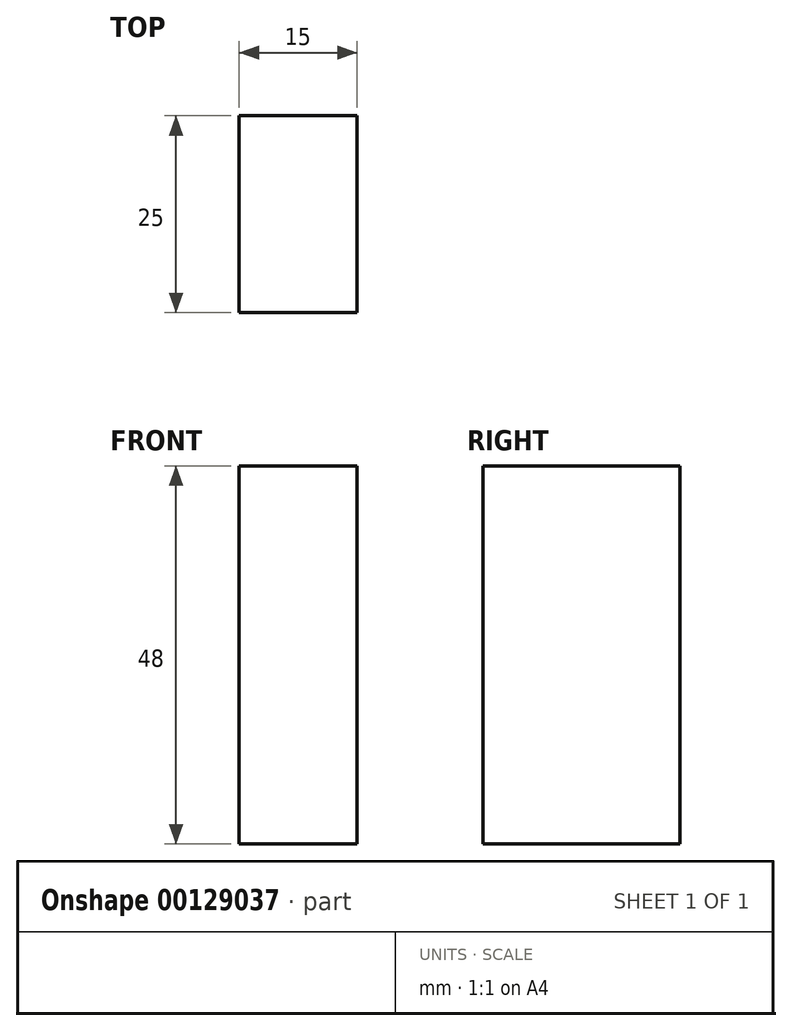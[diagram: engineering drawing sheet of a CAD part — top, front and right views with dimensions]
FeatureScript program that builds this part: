
annotation { "Feature Type Name" : "Feature", "Feature Type Description" : "" }
export const myFeature = defineFeature(function(context is Context, id is Id, definition is map)
    precondition{}
    {
        {
            var Q0;
            Q0=qCreatedBy(makeId("Top.planeOp"),FACE);
            var sketch = newSketch(context, id + "F0", { "sketchPlane" : qUnion([Q0])});
            skLineSegment(sketch, "E0.bottom", {"start": v(-13.79, 27.47) * mm, "end": v(1.21, 27.47) * mm});
            skLineSegment(sketch, "E0.top", {"start": v(-13.79, 2.47) * mm, "end": v(1.21, 2.47) * mm});
            skLineSegment(sketch, "E0.left", {"start": v(-13.79, 27.47) * mm, "end": v(-13.79, 2.47) * mm});
            skLineSegment(sketch, "E0.right", {"start": v(1.21, 27.47) * mm, "end": v(1.21, 2.47) * mm});
            skSolve(sketch);
        }
        {
            var Q0;
            Q0=makeQuery(id+"F0.imprint","IMPRINT",FACE,{"disambiguationData":[TD([[makeQuery(id+"F0.imprint","IMPRINT",EDGE,{"derivedFrom":sQuery(id+"F0.wireOp",EDGE,"E0.bottom")}),-1.0]])]});
            extrude(context, id + "F1", {"entities" : qUnion([Q0]), "depth" : 48 * mm});
        }
    });
